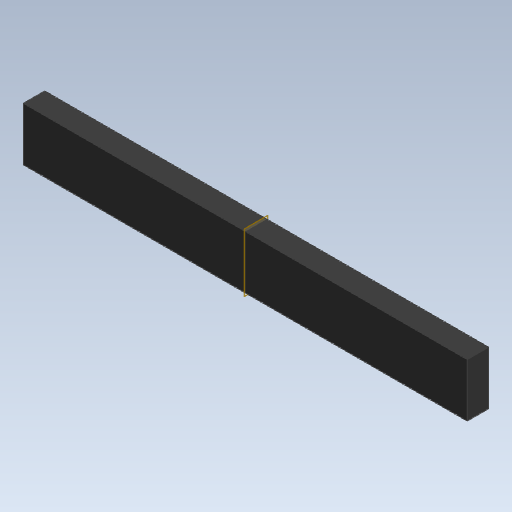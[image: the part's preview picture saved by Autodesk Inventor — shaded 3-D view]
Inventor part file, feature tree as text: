
AUTODESK INVENTOR PART (.ipt)
format: ipt  version: 2020 (Build 240168000, 168)  size: 98,304 bytes
history: native  units: mm
features: other x1, extrude x1
ambient origin geometry x8: Origin, YZ Plane, XZ Plane, XY Plane, X Axis, Y Axis, Z Axis, Center Point
bodies: Body1 (feature_tree)
feature tree (2):
  other  "實體1"
  extrude  "擠出1"  Depth=15.0mm
